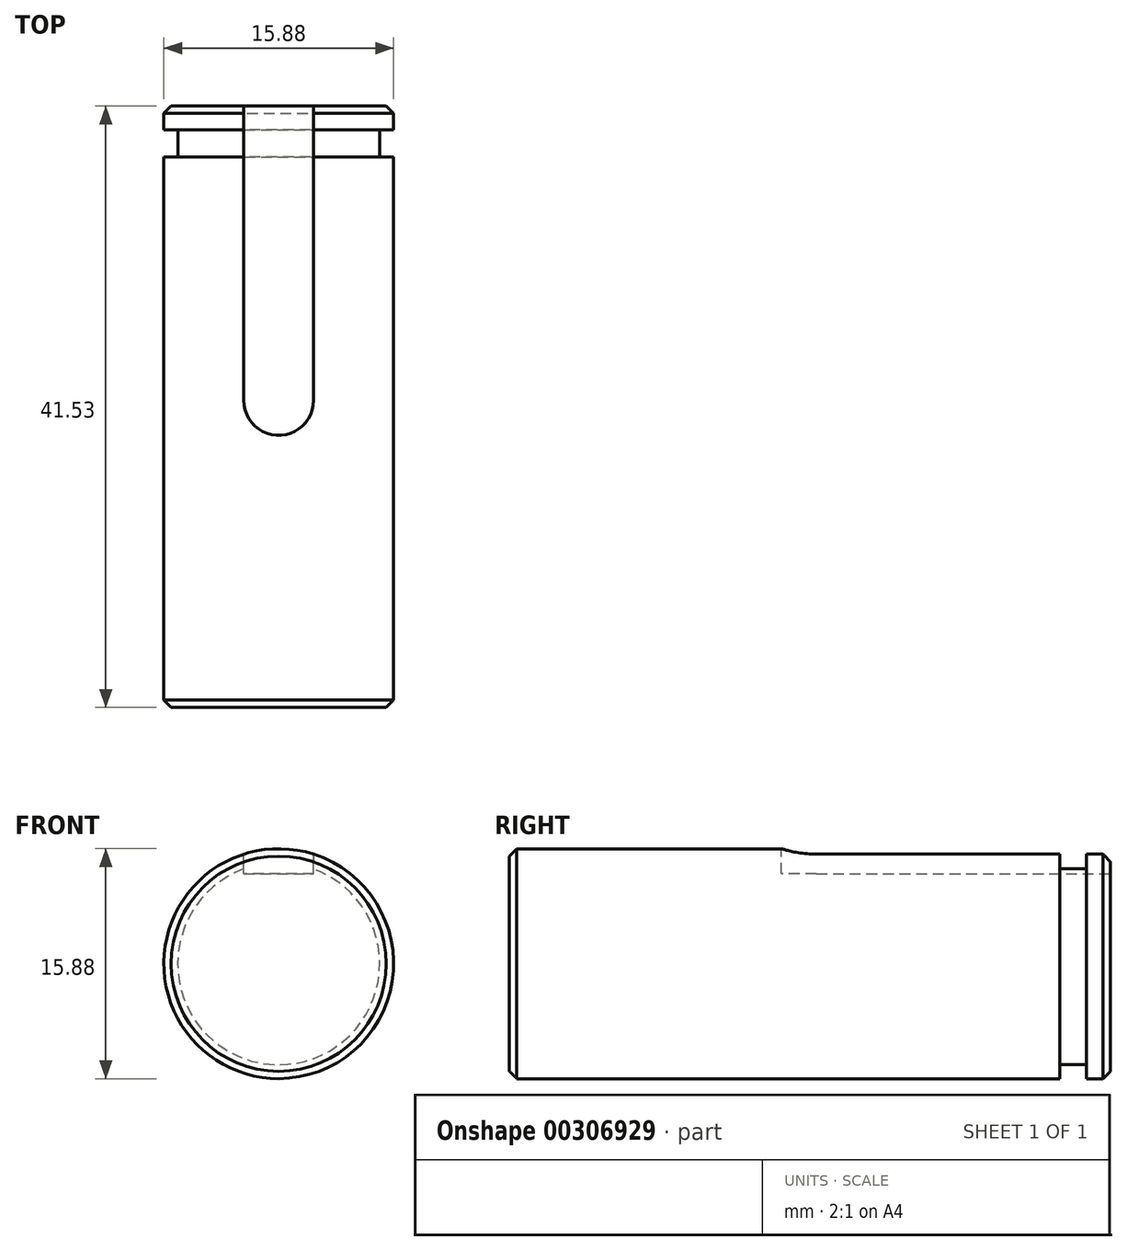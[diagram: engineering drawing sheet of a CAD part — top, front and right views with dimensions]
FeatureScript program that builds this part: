
annotation { "Feature Type Name" : "Feature", "Feature Type Description" : "" }
export const myFeature = defineFeature(function(context is Context, id is Id, definition is map)
    precondition{}
    {
        {
            var Q0;
            Q0=qCreatedBy(makeId("Front.planeOp"),FACE);
            var sketch = newSketch(context, id + "F0", { "sketchPlane" : qUnion([Q0])});
            skCircle(sketch, "E0", {"center": v(0, 0) * mm, "radius": 7.94 * mm});
            skSolve(sketch);
        }
        {
            var Q0;
            Q0=makeQuery(id+"F0.imprint","IMPRINT",FACE,{"disambiguationData":[TD([[makeQuery(id+"F0.imprint","IMPRINT",EDGE,{"derivedFrom":sQuery(id+"F0.wireOp",EDGE,"E0")}),1.0]])]});
            extrude(context, id + "F1", {"entities" : qUnion([Q0]), "depth" : 41.53 * mm});
        }
        {
            var Q0;
            Q0=qCreatedBy(makeId("Top.planeOp"),FACE);
            cPlane(context, id + "F2", {"entities" : qUnion([Q0]), "cplaneType" : CPlaneType.OFFSET, "offset" : 9.4 * mm, "width" : 152.4 * mm, "height" : 152.4 * mm});
        }
        {
            var Q0;
            Q0=qCreatedBy(id+"F2.planeOp",FACE);
            var sketch = newSketch(context, id + "F3", { "sketchPlane" : qUnion([Q0])});
            skLineSegment(sketch, "E1.top", {"start": v(2.41, 0) * mm, "end": v(-2.41, 0) * mm});
            skLineSegment(sketch, "E1.left", {"start": v(2.41, -20.32) * mm, "end": v(2.41, 0) * mm});
            skLineSegment(sketch, "E1.right", {"start": v(-2.41, -20.32) * mm, "end": v(-2.41, 0) * mm});
            skPoint(sketch, "E1.middle", {"position": v(0, 0) * mm});
            skArc(sketch, "E2", {"start": v(-2.41, -20.32) * mm, "mid": v(0, -22.73) * mm, "end": v(2.41, -20.32) * mm});
            skSolve(sketch);
        }
        {
            var Q0;
            Q0=makeQuery(id+"F3.imprint","IMPRINT",FACE,{"disambiguationData":[TD([[makeQuery(id+"F3.imprint","IMPRINT",EDGE,{"derivedFrom":sQuery(id+"F3.wireOp",EDGE,"E1.top")}),1.0]])]});
            extrude(context, id + "F4", {"entities" : qUnion([Q0]), "operationType" : NewBodyOperationType.REMOVE, "oppositeDirection" : true, "depth" : 3.17 * mm});
        }
        {
            var Q0;
            Q0=qCreatedBy(makeId("Right.planeOp"),FACE);
            var sketch = newSketch(context, id + "F5", { "sketchPlane" : qUnion([Q0])});
            skLineSegment(sketch, "E3.bottom", {"start": v(-1.65, 10.02) * mm, "end": v(-3.5, 10.02) * mm});
            skLineSegment(sketch, "E3.top", {"start": v(-1.65, 6.98) * mm, "end": v(-3.5, 6.98) * mm});
            skLineSegment(sketch, "E3.left", {"start": v(-1.65, 10.02) * mm, "end": v(-1.65, 6.98) * mm});
            skLineSegment(sketch, "E3.right", {"start": v(-3.5, 10.02) * mm, "end": v(-3.5, 6.98) * mm});
            skSolve(sketch);
        }
        {
            var Q0;
            Q0=makeQuery(id+"F5.imprint","IMPRINT",FACE,{"disambiguationData":[TD([[makeQuery(id+"F5.imprint","IMPRINT",EDGE,{"derivedFrom":sQuery(id+"F5.wireOp",EDGE,"E3.bottom")}),1.0]])]});
            var Q1;
            Q1=sQuery(id+"F0.wireOp",EDGE,"E0");
            revolve(context, id + "F6", {"operationType" : NewBodyOperationType.REMOVE, "entities" : qUnion([Q0]), "axis" : qUnion([Q1]), "revolveType" : RevolveType.FULL, "oppositeDirection" : true});
        }
        {
            var Q0;
            Q0=makeQuery(id+"F1.opExtrude","CAP_EDGE",EDGE,{"disambiguationData":[OSD([sQuery(id+"F0.wireOp",EDGE,"E0")])],"isStart":false});
            var Q1;
            Q1=makeQuery(id+"F1.opExtrude","CAP_EDGE",EDGE,{"disambiguationData":[OSD([sQuery(id+"F0.wireOp",EDGE,"E0")])],"isStart":true});
            chamfer(context, id + "F7", {"entities" : qUnion([Q0, Q1]), "width" : 0.5 * mm, "tangentPropagation" : true});
        }
    });
